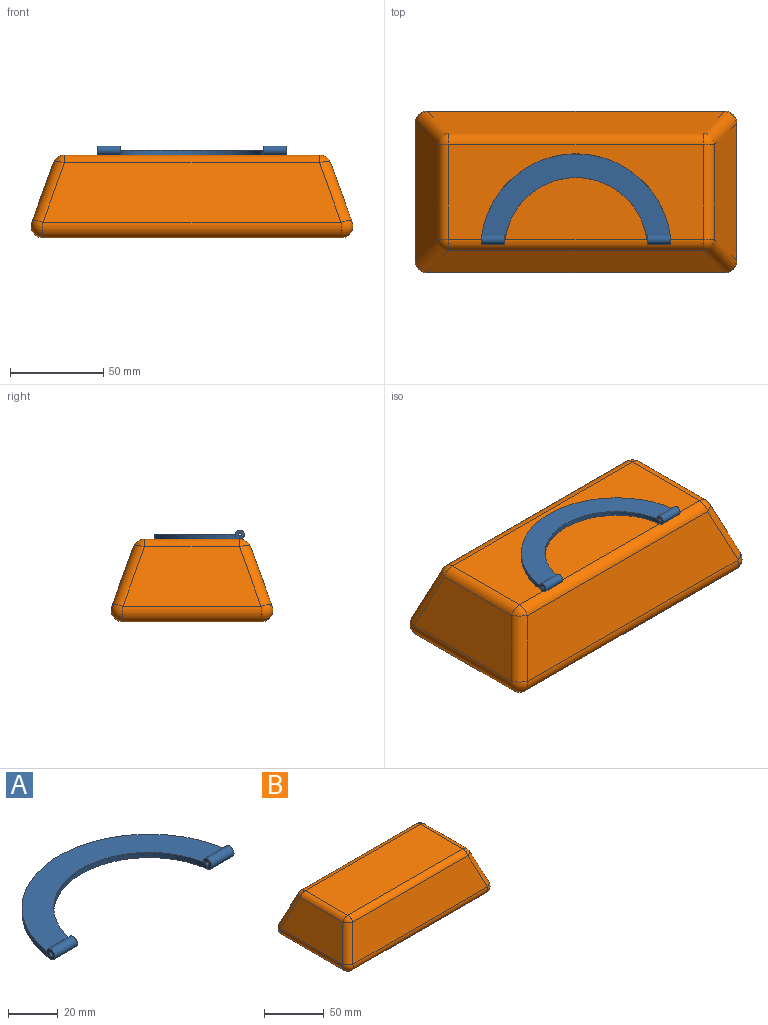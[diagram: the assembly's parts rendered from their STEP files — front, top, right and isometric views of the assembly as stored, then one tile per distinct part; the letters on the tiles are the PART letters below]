
ASSEMBLY  parts=2 mates=1
PART A: 14 faces, bbox 101.6x48.4x4.8 mm
  f0: plane 1.52x0.08mm, normal (0,-1,0), area 0.1mm2, adj f2,f5,f10,f13
  f1: plane 101x45.09mm, normal (0,0,1), area 1593.5mm2, adj f2,f3,f6,f7,f9,f10,f11,f13
  f2: cylinder r=38.35mm len=76.03mm, axis (0,0,-1), area 278.7mm2, adj f0,f1,f4,f5,f9,f13
  f3: cylinder r=51.05mm len=101.6mm, axis (0,0,-1), area 371.7mm2, adj f1,f5,f6,f11
  f4: plane 1.52x0.08mm, normal (0,-1,0), area 0.1mm2, adj f2,f5,f7,f9
  f5: plane 101.6x45.97mm, normal (0,0,-1), area 1654.3mm2, adj f0,f2,f3,f4,f6,f11
  f6: cylinder r=2.41mm len=12.7mm, axis (1,0,0), area 143.5mm2, adj f1,f3,f5,f7,f8
  f7: plane 4.83x4.82mm, normal (-1,0,0), area 11.7mm2, adj f1,f4,f6,f9
  f8: plane 4.83x4.83mm, normal (1,0,0), area 15.8mm2, adj f6,f9
  f9: cylinder r=0.89mm len=12.91mm, axis (1,0,0), area 71.2mm2, adj f1,f2,f4,f7,f8
  f10: plane 4.83x4.82mm, normal (1,0,0), area 11.7mm2, adj f0,f1,f11,f13
  f11: cylinder r=2.41mm len=12.7mm, axis (-1,0,0), area 143.5mm2, adj f1,f3,f5,f10,f12
  f12: plane 4.83x4.83mm, normal (-1,0,0), area 15.8mm2, adj f11,f13
  f13: cylinder r=0.89mm len=12.91mm, axis (-1,0,0), area 71.2mm2, adj f0,f1,f2,f10,f12
PART B: 26 faces, bbox 172.4x86.6x44.5 mm
  f0: plane 159.66x31.75mm, normal (0,0.94,0.34), area 5004.2mm2, adj f14,f19,f22,f25
  f1: plane 73.94x31.75mm, normal (-0.94,0,0.34), area 2107.7mm2, adj f11,f20,f21,f25
  f2: plane 159.66x31.75mm, normal (0,-0.94,0.34), area 5004.2mm2, adj f6,f10,f11,f12
  f3: plane 73.94x31.75mm, normal (0.94,0,0.34), area 2107.7mm2, adj f6,f9,f13,f14
  f4: plane 136.55x50.83mm, normal (0,0,1), area 6940.2mm2, adj f9,f10,f19,f20
  f5: plane 159.66x73.94mm, normal (0,0,-1), area 11805.1mm2, adj f12,f13,f21,f22
  f6: cylinder r=6.35mm len=32.48mm, axis (0.32,-0.32,-0.89), area 329.6mm2, adj f2,f3,f7,f8
  f7: sphere r=6.35mm, area 36.8mm2, adj f6,f9,f10
  f8: sphere r=6.35mm, area 89.9mm2, adj f6,f12,f13
  f9: cylinder r=6.35mm len=50.83mm, axis (0,-1,0), area 394.3mm2, adj f3,f4,f7,f15
  f10: cylinder r=6.35mm len=136.55mm, axis (1,0,0), area 1059.4mm2, adj f2,f4,f7,f16
  f11: cylinder r=6.35mm len=32.48mm, axis (-0.32,-0.32,-0.89), area 329.6mm2, adj f1,f2,f16,f17
  f12: cylinder r=6.35mm len=159.66mm, axis (-1,0,0), area 1946.5mm2, adj f2,f5,f8,f17
  f13: cylinder r=6.35mm len=73.94mm, axis (0,1,0), area 901.4mm2, adj f3,f5,f8,f18
  f14: cylinder r=6.35mm len=32.48mm, axis (0.32,0.32,-0.89), area 329.6mm2, adj f0,f3,f15,f18
  f15: sphere r=6.35mm, area 36.8mm2, adj f9,f14,f19
  f16: sphere r=6.35mm, area 36.8mm2, adj f10,f11,f20
  f17: sphere r=6.35mm, area 89.9mm2, adj f11,f12,f21
  f18: sphere r=6.35mm, area 89.9mm2, adj f13,f14,f22
  f19: cylinder r=6.35mm len=136.55mm, axis (1,0,0), area 1059.4mm2, adj f0,f4,f15,f23
  f20: cylinder r=6.35mm len=50.83mm, axis (0,-1,0), area 394.3mm2, adj f1,f4,f16,f23
  f21: cylinder r=6.35mm len=73.94mm, axis (0,1,0), area 901.4mm2, adj f1,f5,f17,f24
  f22: cylinder r=6.35mm len=159.66mm, axis (-1,0,0), area 1946.5mm2, adj f0,f5,f18,f24
  f23: sphere r=6.35mm, area 36.8mm2, adj f19,f20,f25
  f24: sphere r=6.35mm, area 89.9mm2, adj f21,f22,f25
  f25: cylinder r=6.35mm len=32.48mm, axis (-0.32,0.32,-0.89), area 329.6mm2, adj f0,f1,f23,f24
PLACE A t=(-25.09,-25.49,51.76)mm
PLACE B t=(-25.09,5.2,7.31)mm
MATE fastened A.f5 <-> B.f4  axis (0,0,-1) through (-25.09,5.2,51.76)mm
